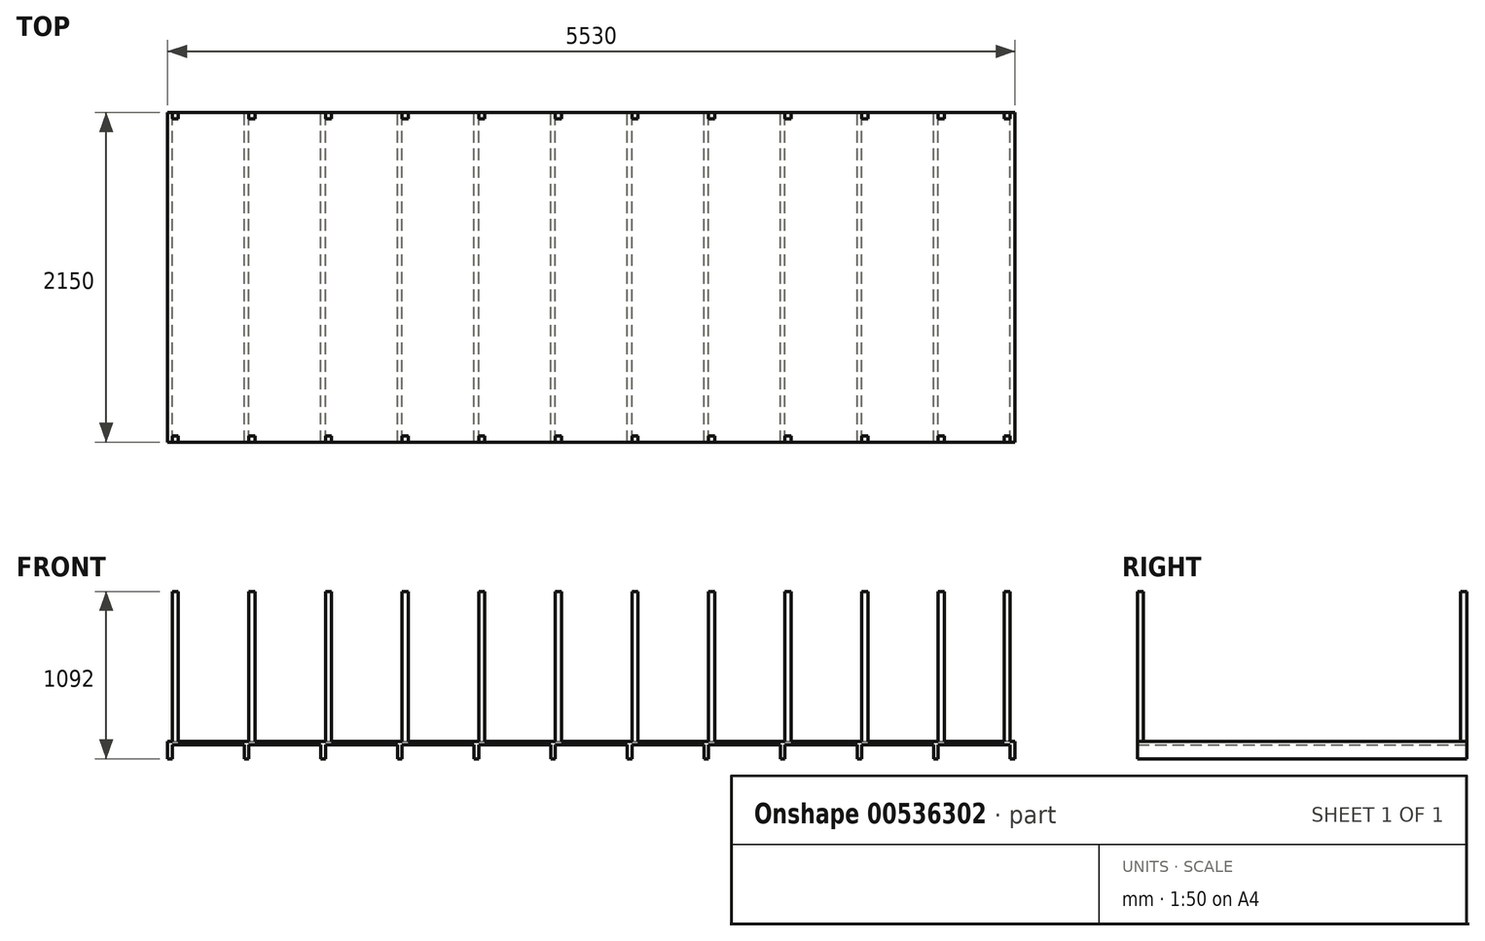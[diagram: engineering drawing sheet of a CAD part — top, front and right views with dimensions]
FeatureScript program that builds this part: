
annotation { "Feature Type Name" : "Feature", "Feature Type Description" : "" }
export const myFeature = defineFeature(function(context is Context, id is Id, definition is map)
    precondition{}
    {
        {
            var Q0;
            Q0=qCreatedBy(makeId("Top.planeOp"),FACE);
            var sketch = newSketch(context, id + "F0", { "sketchPlane" : qUnion([Q0])});
            skLineSegment(sketch, "E0.bottom", {"start": v(-152.5, -84.62) * mm, "end": v(5347.5, -84.62) * mm});
            skLineSegment(sketch, "E0.top", {"start": v(-152.5, 2065.38) * mm, "end": v(5347.5, 2065.38) * mm});
            skLineSegment(sketch, "E0.left", {"start": v(-152.5, -84.62) * mm, "end": v(-152.5, 2065.38) * mm});
            skLineSegment(sketch, "E0.right", {"start": v(5347.5, -84.62) * mm, "end": v(5347.5, 2065.38) * mm});
            skLineSegment(sketch, "E1.0", {"start": v(-122.5, -84.62) * mm, "end": v(-122.5, 2065.38) * mm});
            skLineSegment(sketch, "E2.1.0.0", {"start": v(377.5, -84.62) * mm, "end": v(377.5, 2065.38) * mm});
            skLineSegment(sketch, "E2.1.0.1", {"start": v(347.5, -84.62) * mm, "end": v(347.5, 2065.38) * mm});
            skLineSegment(sketch, "E2.2.0.0", {"start": v(877.5, -84.62) * mm, "end": v(877.5, 2065.38) * mm});
            skLineSegment(sketch, "E2.2.0.1", {"start": v(847.5, -84.62) * mm, "end": v(847.5, 2065.38) * mm});
            skLineSegment(sketch, "E2.3.0.0", {"start": v(1377.5, -84.62) * mm, "end": v(1377.5, 2065.38) * mm});
            skLineSegment(sketch, "E2.3.0.1", {"start": v(1347.5, -84.62) * mm, "end": v(1347.5, 2065.38) * mm});
            skLineSegment(sketch, "E2.4.0.0", {"start": v(1877.5, -84.62) * mm, "end": v(1877.5, 2065.38) * mm});
            skLineSegment(sketch, "E2.4.0.1", {"start": v(1847.5, -84.62) * mm, "end": v(1847.5, 2065.38) * mm});
            skLineSegment(sketch, "E2.5.0.0", {"start": v(2377.5, -84.62) * mm, "end": v(2377.5, 2065.38) * mm});
            skLineSegment(sketch, "E2.5.0.1", {"start": v(2347.5, -84.62) * mm, "end": v(2347.5, 2065.38) * mm});
            skLineSegment(sketch, "E2.6.0.0", {"start": v(2877.5, -84.62) * mm, "end": v(2877.5, 2065.38) * mm});
            skLineSegment(sketch, "E2.6.0.1", {"start": v(2847.5, -84.62) * mm, "end": v(2847.5, 2065.38) * mm});
            skLineSegment(sketch, "E2.7.0.0", {"start": v(3377.5, -84.62) * mm, "end": v(3377.5, 2065.38) * mm});
            skLineSegment(sketch, "E2.7.0.1", {"start": v(3347.5, -84.62) * mm, "end": v(3347.5, 2065.38) * mm});
            skLineSegment(sketch, "E2.8.0.0", {"start": v(3877.5, -84.62) * mm, "end": v(3877.5, 2065.38) * mm});
            skLineSegment(sketch, "E2.8.0.1", {"start": v(3847.5, -84.62) * mm, "end": v(3847.5, 2065.38) * mm});
            skLineSegment(sketch, "E2.9.0.0", {"start": v(4377.5, -84.62) * mm, "end": v(4377.5, 2065.38) * mm});
            skLineSegment(sketch, "E2.9.0.1", {"start": v(4347.5, -84.62) * mm, "end": v(4347.5, 2065.38) * mm});
            skLineSegment(sketch, "E2.10.0.0", {"start": v(4877.5, -84.62) * mm, "end": v(4877.5, 2065.38) * mm});
            skLineSegment(sketch, "E2.10.0.1", {"start": v(4847.5, -84.62) * mm, "end": v(4847.5, 2065.38) * mm});
            skLineSegment(sketch, "E2.11.0.0", {"start": v(5377.5, -84.62) * mm, "end": v(5377.5, 2065.38) * mm});
            skLineSegment(sketch, "E2.direction1", {"start": v(-152.5, -84.62) * mm, "end": v(347.5, -84.62) * mm, "construction": true});
            skLineSegment(sketch, "E3", {"start": v(5347.5, -84.62) * mm, "end": v(5377.5, -84.62) * mm});
            skLineSegment(sketch, "E4", {"start": v(5377.5, 2065.38) * mm, "end": v(5347.5, 2065.38) * mm});
            skSolve(sketch);
        }
        {
            var Q0;
            Q0 = qSketchRegion(id + "F0", true);
            extrude(context, id + "F1", {"entities" : qUnion([Q0]), "depth" : 22 * mm, "offsetDistance" : 25 * mm});
        }
        {
            var Q0;
            {var subQ0=sQuery(id+"F0.wireOp",EDGE,"E0.left");Q0=makeQuery(id+"F0.imprint","IMPRINT",FACE,{"disambiguationData":[TD([[makeQuery(id+"F0.imprint","IMPRINT",EDGE,{"derivedFrom":subQ0}),-1.0]])]});}
            var Q1;
            {var subQ0=sQuery(id+"F0.wireOp",EDGE,"E2.1.0.0");Q1=makeQuery(id+"F0.imprint","IMPRINT",FACE,{"disambiguationData":[TD([[makeQuery(id+"F0.imprint","IMPRINT",EDGE,{"derivedFrom":subQ0}),1.0]])]});}
            var Q2;
            {var subQ0=sQuery(id+"F0.wireOp",EDGE,"E2.2.0.0");Q2=makeQuery(id+"F0.imprint","IMPRINT",FACE,{"disambiguationData":[TD([[makeQuery(id+"F0.imprint","IMPRINT",EDGE,{"derivedFrom":subQ0}),1.0]])]});}
            var Q3;
            {var subQ0=sQuery(id+"F0.wireOp",EDGE,"E2.3.0.0");Q3=makeQuery(id+"F0.imprint","IMPRINT",FACE,{"disambiguationData":[TD([[makeQuery(id+"F0.imprint","IMPRINT",EDGE,{"derivedFrom":subQ0}),1.0]])]});}
            var Q4;
            {var subQ0=sQuery(id+"F0.wireOp",EDGE,"E2.4.0.0");Q4=makeQuery(id+"F0.imprint","IMPRINT",FACE,{"disambiguationData":[TD([[makeQuery(id+"F0.imprint","IMPRINT",EDGE,{"derivedFrom":subQ0}),1.0]])]});}
            var Q5;
            {var subQ0=sQuery(id+"F0.wireOp",EDGE,"E2.5.0.0");Q5=makeQuery(id+"F0.imprint","IMPRINT",FACE,{"disambiguationData":[TD([[makeQuery(id+"F0.imprint","IMPRINT",EDGE,{"derivedFrom":subQ0}),1.0]])]});}
            var Q6;
            {var subQ0=sQuery(id+"F0.wireOp",EDGE,"E2.6.0.0");Q6=makeQuery(id+"F0.imprint","IMPRINT",FACE,{"disambiguationData":[TD([[makeQuery(id+"F0.imprint","IMPRINT",EDGE,{"derivedFrom":subQ0}),1.0]])]});}
            var Q7;
            {var subQ0=sQuery(id+"F0.wireOp",EDGE,"E2.7.0.0");Q7=makeQuery(id+"F0.imprint","IMPRINT",FACE,{"disambiguationData":[TD([[makeQuery(id+"F0.imprint","IMPRINT",EDGE,{"derivedFrom":subQ0}),1.0]])]});}
            var Q8;
            {var subQ0=sQuery(id+"F0.wireOp",EDGE,"E2.8.0.0");Q8=makeQuery(id+"F0.imprint","IMPRINT",FACE,{"disambiguationData":[TD([[makeQuery(id+"F0.imprint","IMPRINT",EDGE,{"derivedFrom":subQ0}),1.0]])]});}
            var Q9;
            {var subQ0=sQuery(id+"F0.wireOp",EDGE,"E2.9.0.0");Q9=makeQuery(id+"F0.imprint","IMPRINT",FACE,{"disambiguationData":[TD([[makeQuery(id+"F0.imprint","IMPRINT",EDGE,{"derivedFrom":subQ0}),1.0]])]});}
            var Q10;
            {var subQ0=sQuery(id+"F0.wireOp",EDGE,"E2.10.0.0");Q10=makeQuery(id+"F0.imprint","IMPRINT",FACE,{"disambiguationData":[TD([[makeQuery(id+"F0.imprint","IMPRINT",EDGE,{"derivedFrom":subQ0}),1.0]])]});}
            var Q11;
            Q11=makeQuery(id+"F0.imprint","IMPRINT",FACE,{"disambiguationData":[TD([[makeQuery(id+"F0.imprint","IMPRINT",EDGE,{"derivedFrom":sQuery(id+"F0.wireOp",EDGE,"E2.11.0.0")}),1.0]])]});
            extrude(context, id + "F2", {"entities" : qUnion([Q0, Q1, Q2, Q3, Q4, Q5, Q6, Q7, Q8, Q9, Q10, Q11]), "operationType" : NewBodyOperationType.ADD, "oppositeDirection" : true, "depth" : 90 * mm, "offsetDistance" : 25 * mm});
        }
        {
            var Q0;
            Q0=makeQuery(id+"F1.opExtrude","CAP_FACE",FACE,{"disambiguationData":[OSD([sQuery(id+"F0.wireOp",EDGE,"E0.bottom"),sQuery(id+"F0.wireOp",EDGE,"E0.top"),sQuery(id+"F0.wireOp",EDGE,"E0.left"),sQuery(id+"F0.wireOp",EDGE,"E2.11.0.0"),sQuery(id+"F0.wireOp",EDGE,"E3"),sQuery(id+"F0.wireOp",EDGE,"E4")])],"isStart":false});
            var sketch = newSketch(context, id + "F3", { "sketchPlane" : qUnion([Q0])});
            skLineSegment(sketch, "E5", {"start": v(-152.5, -84.62) * mm, "end": v(-122.5, -84.62) * mm});
            skLineSegment(sketch, "E6.bottom", {"start": v(-122.5, -84.62) * mm, "end": v(-82.5, -84.62) * mm});
            skLineSegment(sketch, "E6.top", {"start": v(-122.5, -44.62) * mm, "end": v(-82.5, -44.62) * mm});
            skLineSegment(sketch, "E6.left", {"start": v(-122.5, -84.62) * mm, "end": v(-122.5, -44.62) * mm});
            skLineSegment(sketch, "E6.right", {"start": v(-82.5, -84.62) * mm, "end": v(-82.5, -44.62) * mm});
            skLineSegment(sketch, "E7.MirrorCS", {"start": v(-122.5, 2065.38) * mm, "end": v(-122.5, 2025.38) * mm});
            skLineSegment(sketch, "E8.MirrorCS", {"start": v(-122.5, 2065.38) * mm, "end": v(-82.5, 2065.38) * mm});
            skLineSegment(sketch, "E9.MirrorCS", {"start": v(-122.5, 2025.38) * mm, "end": v(-82.5, 2025.38) * mm});
            skLineSegment(sketch, "E10.MirrorCS", {"start": v(-82.5, 2065.38) * mm, "end": v(-82.5, 2025.38) * mm});
            skLineSegment(sketch, "E11.MirrorCS", {"start": v(5347.5, -44.62) * mm, "end": v(5307.5, -44.62) * mm});
            skLineSegment(sketch, "E12.MirrorCS", {"start": v(5307.5, -84.62) * mm, "end": v(5307.5, -44.62) * mm});
            skLineSegment(sketch, "E13.MirrorCS", {"start": v(5347.5, -84.62) * mm, "end": v(5307.5, -84.62) * mm});
            skLineSegment(sketch, "E14.MirrorCS", {"start": v(5347.5, -84.62) * mm, "end": v(5347.5, -44.62) * mm});
            skLineSegment(sketch, "E15.MirrorCS", {"start": v(5347.5, 2065.38) * mm, "end": v(5307.5, 2065.38) * mm});
            skLineSegment(sketch, "E16.MirrorCS", {"start": v(5347.5, 2065.38) * mm, "end": v(5347.5, 2025.38) * mm});
            skLineSegment(sketch, "E17.MirrorCS", {"start": v(5347.5, 2025.38) * mm, "end": v(5307.5, 2025.38) * mm});
            skLineSegment(sketch, "E18.MirrorCS", {"start": v(5307.5, 2065.38) * mm, "end": v(5307.5, 2025.38) * mm});
            skLineSegment(sketch, "E19.1.0.0", {"start": v(377.5, 2025.38) * mm, "end": v(417.5, 2025.38) * mm});
            skLineSegment(sketch, "E19.1.0.1", {"start": v(417.5, 2065.38) * mm, "end": v(417.5, 2025.38) * mm});
            skLineSegment(sketch, "E19.1.0.2", {"start": v(377.5, 2065.38) * mm, "end": v(417.5, 2065.38) * mm});
            skLineSegment(sketch, "E19.1.0.3", {"start": v(377.5, 2065.38) * mm, "end": v(377.5, 2025.38) * mm});
            skLineSegment(sketch, "E19.1.0.4", {"start": v(377.5, -44.62) * mm, "end": v(417.5, -44.62) * mm});
            skLineSegment(sketch, "E19.1.0.5", {"start": v(377.5, -84.62) * mm, "end": v(377.5, -44.62) * mm});
            skLineSegment(sketch, "E19.1.0.6", {"start": v(377.5, -84.62) * mm, "end": v(417.5, -84.62) * mm});
            skLineSegment(sketch, "E19.1.0.7", {"start": v(417.5, -84.62) * mm, "end": v(417.5, -44.62) * mm});
            skLineSegment(sketch, "E19.2.0.0", {"start": v(877.5, 2025.38) * mm, "end": v(917.5, 2025.38) * mm});
            skLineSegment(sketch, "E19.2.0.1", {"start": v(917.5, 2065.38) * mm, "end": v(917.5, 2025.38) * mm});
            skLineSegment(sketch, "E19.2.0.2", {"start": v(877.5, 2065.38) * mm, "end": v(917.5, 2065.38) * mm});
            skLineSegment(sketch, "E19.2.0.3", {"start": v(877.5, 2065.38) * mm, "end": v(877.5, 2025.38) * mm});
            skLineSegment(sketch, "E19.2.0.4", {"start": v(877.5, -44.62) * mm, "end": v(917.5, -44.62) * mm});
            skLineSegment(sketch, "E19.2.0.5", {"start": v(877.5, -84.62) * mm, "end": v(877.5, -44.62) * mm});
            skLineSegment(sketch, "E19.2.0.6", {"start": v(877.5, -84.62) * mm, "end": v(917.5, -84.62) * mm});
            skLineSegment(sketch, "E19.2.0.7", {"start": v(917.5, -84.62) * mm, "end": v(917.5, -44.62) * mm});
            skLineSegment(sketch, "E19.3.0.0", {"start": v(1377.5, 2025.38) * mm, "end": v(1417.5, 2025.38) * mm});
            skLineSegment(sketch, "E19.3.0.1", {"start": v(1417.5, 2065.38) * mm, "end": v(1417.5, 2025.38) * mm});
            skLineSegment(sketch, "E19.3.0.2", {"start": v(1377.5, 2065.38) * mm, "end": v(1417.5, 2065.38) * mm});
            skLineSegment(sketch, "E19.3.0.3", {"start": v(1377.5, 2065.38) * mm, "end": v(1377.5, 2025.38) * mm});
            skLineSegment(sketch, "E19.3.0.4", {"start": v(1377.5, -44.62) * mm, "end": v(1417.5, -44.62) * mm});
            skLineSegment(sketch, "E19.3.0.5", {"start": v(1377.5, -84.62) * mm, "end": v(1377.5, -44.62) * mm});
            skLineSegment(sketch, "E19.3.0.6", {"start": v(1377.5, -84.62) * mm, "end": v(1417.5, -84.62) * mm});
            skLineSegment(sketch, "E19.3.0.7", {"start": v(1417.5, -84.62) * mm, "end": v(1417.5, -44.62) * mm});
            skLineSegment(sketch, "E19.4.0.0", {"start": v(1877.5, 2025.38) * mm, "end": v(1917.5, 2025.38) * mm});
            skLineSegment(sketch, "E19.4.0.1", {"start": v(1917.5, 2065.38) * mm, "end": v(1917.5, 2025.38) * mm});
            skLineSegment(sketch, "E19.4.0.2", {"start": v(1877.5, 2065.38) * mm, "end": v(1917.5, 2065.38) * mm});
            skLineSegment(sketch, "E19.4.0.3", {"start": v(1877.5, 2065.38) * mm, "end": v(1877.5, 2025.38) * mm});
            skLineSegment(sketch, "E19.4.0.4", {"start": v(1877.5, -44.62) * mm, "end": v(1917.5, -44.62) * mm});
            skLineSegment(sketch, "E19.4.0.5", {"start": v(1877.5, -84.62) * mm, "end": v(1877.5, -44.62) * mm});
            skLineSegment(sketch, "E19.4.0.6", {"start": v(1877.5, -84.62) * mm, "end": v(1917.5, -84.62) * mm});
            skLineSegment(sketch, "E19.4.0.7", {"start": v(1917.5, -84.62) * mm, "end": v(1917.5, -44.62) * mm});
            skLineSegment(sketch, "E19.5.0.0", {"start": v(2377.5, 2025.38) * mm, "end": v(2417.5, 2025.38) * mm});
            skLineSegment(sketch, "E19.5.0.1", {"start": v(2417.5, 2065.38) * mm, "end": v(2417.5, 2025.38) * mm});
            skLineSegment(sketch, "E19.5.0.2", {"start": v(2377.5, 2065.38) * mm, "end": v(2417.5, 2065.38) * mm});
            skLineSegment(sketch, "E19.5.0.3", {"start": v(2377.5, 2065.38) * mm, "end": v(2377.5, 2025.38) * mm});
            skLineSegment(sketch, "E19.5.0.4", {"start": v(2377.5, -44.62) * mm, "end": v(2417.5, -44.62) * mm});
            skLineSegment(sketch, "E19.5.0.5", {"start": v(2377.5, -84.62) * mm, "end": v(2377.5, -44.62) * mm});
            skLineSegment(sketch, "E19.5.0.6", {"start": v(2377.5, -84.62) * mm, "end": v(2417.5, -84.62) * mm});
            skLineSegment(sketch, "E19.5.0.7", {"start": v(2417.5, -84.62) * mm, "end": v(2417.5, -44.62) * mm});
            skLineSegment(sketch, "E19.6.0.0", {"start": v(2877.5, 2025.38) * mm, "end": v(2917.5, 2025.38) * mm});
            skLineSegment(sketch, "E19.6.0.1", {"start": v(2917.5, 2065.38) * mm, "end": v(2917.5, 2025.38) * mm});
            skLineSegment(sketch, "E19.6.0.2", {"start": v(2877.5, 2065.38) * mm, "end": v(2917.5, 2065.38) * mm});
            skLineSegment(sketch, "E19.6.0.3", {"start": v(2877.5, 2065.38) * mm, "end": v(2877.5, 2025.38) * mm});
            skLineSegment(sketch, "E19.6.0.4", {"start": v(2877.5, -44.62) * mm, "end": v(2917.5, -44.62) * mm});
            skLineSegment(sketch, "E19.6.0.5", {"start": v(2877.5, -84.62) * mm, "end": v(2877.5, -44.62) * mm});
            skLineSegment(sketch, "E19.6.0.6", {"start": v(2877.5, -84.62) * mm, "end": v(2917.5, -84.62) * mm});
            skLineSegment(sketch, "E19.6.0.7", {"start": v(2917.5, -84.62) * mm, "end": v(2917.5, -44.62) * mm});
            skLineSegment(sketch, "E19.7.0.0", {"start": v(3377.5, 2025.38) * mm, "end": v(3417.5, 2025.38) * mm});
            skLineSegment(sketch, "E19.7.0.1", {"start": v(3417.5, 2065.38) * mm, "end": v(3417.5, 2025.38) * mm});
            skLineSegment(sketch, "E19.7.0.2", {"start": v(3377.5, 2065.38) * mm, "end": v(3417.5, 2065.38) * mm});
            skLineSegment(sketch, "E19.7.0.3", {"start": v(3377.5, 2065.38) * mm, "end": v(3377.5, 2025.38) * mm});
            skLineSegment(sketch, "E19.7.0.4", {"start": v(3377.5, -44.62) * mm, "end": v(3417.5, -44.62) * mm});
            skLineSegment(sketch, "E19.7.0.5", {"start": v(3377.5, -84.62) * mm, "end": v(3377.5, -44.62) * mm});
            skLineSegment(sketch, "E19.7.0.6", {"start": v(3377.5, -84.62) * mm, "end": v(3417.5, -84.62) * mm});
            skLineSegment(sketch, "E19.7.0.7", {"start": v(3417.5, -84.62) * mm, "end": v(3417.5, -44.62) * mm});
            skLineSegment(sketch, "E19.8.0.0", {"start": v(3877.5, 2025.38) * mm, "end": v(3917.5, 2025.38) * mm});
            skLineSegment(sketch, "E19.8.0.1", {"start": v(3917.5, 2065.38) * mm, "end": v(3917.5, 2025.38) * mm});
            skLineSegment(sketch, "E19.8.0.2", {"start": v(3877.5, 2065.38) * mm, "end": v(3917.5, 2065.38) * mm});
            skLineSegment(sketch, "E19.8.0.3", {"start": v(3877.5, 2065.38) * mm, "end": v(3877.5, 2025.38) * mm});
            skLineSegment(sketch, "E19.8.0.4", {"start": v(3877.5, -44.62) * mm, "end": v(3917.5, -44.62) * mm});
            skLineSegment(sketch, "E19.8.0.5", {"start": v(3877.5, -84.62) * mm, "end": v(3877.5, -44.62) * mm});
            skLineSegment(sketch, "E19.8.0.6", {"start": v(3877.5, -84.62) * mm, "end": v(3917.5, -84.62) * mm});
            skLineSegment(sketch, "E19.8.0.7", {"start": v(3917.5, -84.62) * mm, "end": v(3917.5, -44.62) * mm});
            skLineSegment(sketch, "E19.9.0.0", {"start": v(4377.5, 2025.38) * mm, "end": v(4417.5, 2025.38) * mm});
            skLineSegment(sketch, "E19.9.0.1", {"start": v(4417.5, 2065.38) * mm, "end": v(4417.5, 2025.38) * mm});
            skLineSegment(sketch, "E19.9.0.2", {"start": v(4377.5, 2065.38) * mm, "end": v(4417.5, 2065.38) * mm});
            skLineSegment(sketch, "E19.9.0.3", {"start": v(4377.5, 2065.38) * mm, "end": v(4377.5, 2025.38) * mm});
            skLineSegment(sketch, "E19.9.0.4", {"start": v(4377.5, -44.62) * mm, "end": v(4417.5, -44.62) * mm});
            skLineSegment(sketch, "E19.9.0.5", {"start": v(4377.5, -84.62) * mm, "end": v(4377.5, -44.62) * mm});
            skLineSegment(sketch, "E19.9.0.6", {"start": v(4377.5, -84.62) * mm, "end": v(4417.5, -84.62) * mm});
            skLineSegment(sketch, "E19.9.0.7", {"start": v(4417.5, -84.62) * mm, "end": v(4417.5, -44.62) * mm});
            skLineSegment(sketch, "E19.10.0.0", {"start": v(4877.5, 2025.38) * mm, "end": v(4917.5, 2025.38) * mm});
            skLineSegment(sketch, "E19.10.0.1", {"start": v(4917.5, 2065.38) * mm, "end": v(4917.5, 2025.38) * mm});
            skLineSegment(sketch, "E19.10.0.2", {"start": v(4877.5, 2065.38) * mm, "end": v(4917.5, 2065.38) * mm});
            skLineSegment(sketch, "E19.10.0.3", {"start": v(4877.5, 2065.38) * mm, "end": v(4877.5, 2025.38) * mm});
            skLineSegment(sketch, "E19.10.0.4", {"start": v(4877.5, -44.62) * mm, "end": v(4917.5, -44.62) * mm});
            skLineSegment(sketch, "E19.10.0.5", {"start": v(4877.5, -84.62) * mm, "end": v(4877.5, -44.62) * mm});
            skLineSegment(sketch, "E19.10.0.6", {"start": v(4877.5, -84.62) * mm, "end": v(4917.5, -84.62) * mm});
            skLineSegment(sketch, "E19.10.0.7", {"start": v(4917.5, -84.62) * mm, "end": v(4917.5, -44.62) * mm});
            skLineSegment(sketch, "E19.direction1", {"start": v(-122.5, 2025.38) * mm, "end": v(377.5, 2025.38) * mm, "construction": true});
            skSolve(sketch);
        }
        {
            var Q0;
            Q0=makeQuery(id+"F3.imprint","IMPRINT",FACE,{"disambiguationData":[TD([[makeQuery(id+"F3.imprint","IMPRINT",EDGE,{"derivedFrom":sQuery(id+"F3.wireOp",EDGE,"E6.bottom")}),1.0]])]});
            var Q1;
            Q1=makeQuery(id+"F3.imprint","IMPRINT",FACE,{"disambiguationData":[TD([[makeQuery(id+"F3.imprint","IMPRINT",EDGE,{"derivedFrom":sQuery(id+"F3.wireOp",EDGE,"E19.1.0.4")}),-1.0]])]});
            var Q2;
            Q2=makeQuery(id+"F3.imprint","IMPRINT",FACE,{"disambiguationData":[TD([[makeQuery(id+"F3.imprint","IMPRINT",EDGE,{"derivedFrom":sQuery(id+"F3.wireOp",EDGE,"E19.2.0.4")}),-1.0]])]});
            var Q3;
            Q3=makeQuery(id+"F3.imprint","IMPRINT",FACE,{"disambiguationData":[TD([[makeQuery(id+"F3.imprint","IMPRINT",EDGE,{"derivedFrom":sQuery(id+"F3.wireOp",EDGE,"E9.MirrorCS")}),1.0]])]});
            var Q4;
            Q4=makeQuery(id+"F3.imprint","IMPRINT",FACE,{"disambiguationData":[TD([[makeQuery(id+"F3.imprint","IMPRINT",EDGE,{"derivedFrom":sQuery(id+"F3.wireOp",EDGE,"E19.1.0.0")}),1.0]])]});
            var Q5;
            Q5=makeQuery(id+"F3.imprint","IMPRINT",FACE,{"disambiguationData":[TD([[makeQuery(id+"F3.imprint","IMPRINT",EDGE,{"derivedFrom":sQuery(id+"F3.wireOp",EDGE,"E19.2.0.0")}),1.0]])]});
            var Q6;
            Q6=makeQuery(id+"F3.imprint","IMPRINT",FACE,{"disambiguationData":[TD([[makeQuery(id+"F3.imprint","IMPRINT",EDGE,{"derivedFrom":sQuery(id+"F3.wireOp",EDGE,"E19.3.0.0")}),1.0]])]});
            var Q7;
            Q7=makeQuery(id+"F3.imprint","IMPRINT",FACE,{"disambiguationData":[TD([[makeQuery(id+"F3.imprint","IMPRINT",EDGE,{"derivedFrom":sQuery(id+"F3.wireOp",EDGE,"E19.4.0.0")}),1.0]])]});
            var Q8;
            Q8=makeQuery(id+"F3.imprint","IMPRINT",FACE,{"disambiguationData":[TD([[makeQuery(id+"F3.imprint","IMPRINT",EDGE,{"derivedFrom":sQuery(id+"F3.wireOp",EDGE,"E19.5.0.0")}),1.0]])]});
            var Q9;
            Q9=makeQuery(id+"F3.imprint","IMPRINT",FACE,{"disambiguationData":[TD([[makeQuery(id+"F3.imprint","IMPRINT",EDGE,{"derivedFrom":sQuery(id+"F3.wireOp",EDGE,"E19.6.0.0")}),1.0]])]});
            var Q10;
            Q10=makeQuery(id+"F3.imprint","IMPRINT",FACE,{"disambiguationData":[TD([[makeQuery(id+"F3.imprint","IMPRINT",EDGE,{"derivedFrom":sQuery(id+"F3.wireOp",EDGE,"E19.7.0.0")}),1.0]])]});
            var Q11;
            Q11=makeQuery(id+"F3.imprint","IMPRINT",FACE,{"disambiguationData":[TD([[makeQuery(id+"F3.imprint","IMPRINT",EDGE,{"derivedFrom":sQuery(id+"F3.wireOp",EDGE,"E19.8.0.0")}),1.0]])]});
            var Q12;
            Q12=makeQuery(id+"F3.imprint","IMPRINT",FACE,{"disambiguationData":[TD([[makeQuery(id+"F3.imprint","IMPRINT",EDGE,{"derivedFrom":sQuery(id+"F3.wireOp",EDGE,"E19.9.0.0")}),1.0]])]});
            var Q13;
            Q13=makeQuery(id+"F3.imprint","IMPRINT",FACE,{"disambiguationData":[TD([[makeQuery(id+"F3.imprint","IMPRINT",EDGE,{"derivedFrom":sQuery(id+"F3.wireOp",EDGE,"E19.10.0.0")}),1.0]])]});
            var Q14;
            Q14=makeQuery(id+"F3.imprint","IMPRINT",FACE,{"disambiguationData":[TD([[makeQuery(id+"F3.imprint","IMPRINT",EDGE,{"derivedFrom":sQuery(id+"F3.wireOp",EDGE,"E15.MirrorCS")}),-1.0]])]});
            var Q15;
            Q15=makeQuery(id+"F3.imprint","IMPRINT",FACE,{"disambiguationData":[TD([[makeQuery(id+"F3.imprint","IMPRINT",EDGE,{"derivedFrom":sQuery(id+"F3.wireOp",EDGE,"E19.3.0.4")}),-1.0]])]});
            var Q16;
            Q16=makeQuery(id+"F3.imprint","IMPRINT",FACE,{"disambiguationData":[TD([[makeQuery(id+"F3.imprint","IMPRINT",EDGE,{"derivedFrom":sQuery(id+"F3.wireOp",EDGE,"E19.4.0.4")}),-1.0]])]});
            var Q17;
            Q17=makeQuery(id+"F3.imprint","IMPRINT",FACE,{"disambiguationData":[TD([[makeQuery(id+"F3.imprint","IMPRINT",EDGE,{"derivedFrom":sQuery(id+"F3.wireOp",EDGE,"E19.5.0.4")}),-1.0]])]});
            var Q18;
            Q18=makeQuery(id+"F3.imprint","IMPRINT",FACE,{"disambiguationData":[TD([[makeQuery(id+"F3.imprint","IMPRINT",EDGE,{"derivedFrom":sQuery(id+"F3.wireOp",EDGE,"E19.6.0.4")}),-1.0]])]});
            var Q19;
            Q19=makeQuery(id+"F3.imprint","IMPRINT",FACE,{"disambiguationData":[TD([[makeQuery(id+"F3.imprint","IMPRINT",EDGE,{"derivedFrom":sQuery(id+"F3.wireOp",EDGE,"E19.7.0.4")}),-1.0]])]});
            var Q20;
            Q20=makeQuery(id+"F3.imprint","IMPRINT",FACE,{"disambiguationData":[TD([[makeQuery(id+"F3.imprint","IMPRINT",EDGE,{"derivedFrom":sQuery(id+"F3.wireOp",EDGE,"E19.8.0.4")}),-1.0]])]});
            var Q21;
            Q21=makeQuery(id+"F3.imprint","IMPRINT",FACE,{"disambiguationData":[TD([[makeQuery(id+"F3.imprint","IMPRINT",EDGE,{"derivedFrom":sQuery(id+"F3.wireOp",EDGE,"E19.9.0.4")}),-1.0]])]});
            var Q22;
            Q22=makeQuery(id+"F3.imprint","IMPRINT",FACE,{"disambiguationData":[TD([[makeQuery(id+"F3.imprint","IMPRINT",EDGE,{"derivedFrom":sQuery(id+"F3.wireOp",EDGE,"E19.10.0.4")}),-1.0]])]});
            var Q23;
            Q23=makeQuery(id+"F3.imprint","IMPRINT",FACE,{"disambiguationData":[TD([[makeQuery(id+"F3.imprint","IMPRINT",EDGE,{"derivedFrom":sQuery(id+"F3.wireOp",EDGE,"E11.MirrorCS")}),1.0]])]});
            extrude(context, id + "F4", {"entities" : qUnion([Q0, Q1, Q2, Q3, Q4, Q5, Q6, Q7, Q8, Q9, Q10, Q11, Q12, Q13, Q14, Q15, Q16, Q17, Q18, Q19, Q20, Q21, Q22, Q23]), "operationType" : NewBodyOperationType.ADD, "depth" : 980 * mm, "offsetDistance" : 25 * mm});
        }
    });
